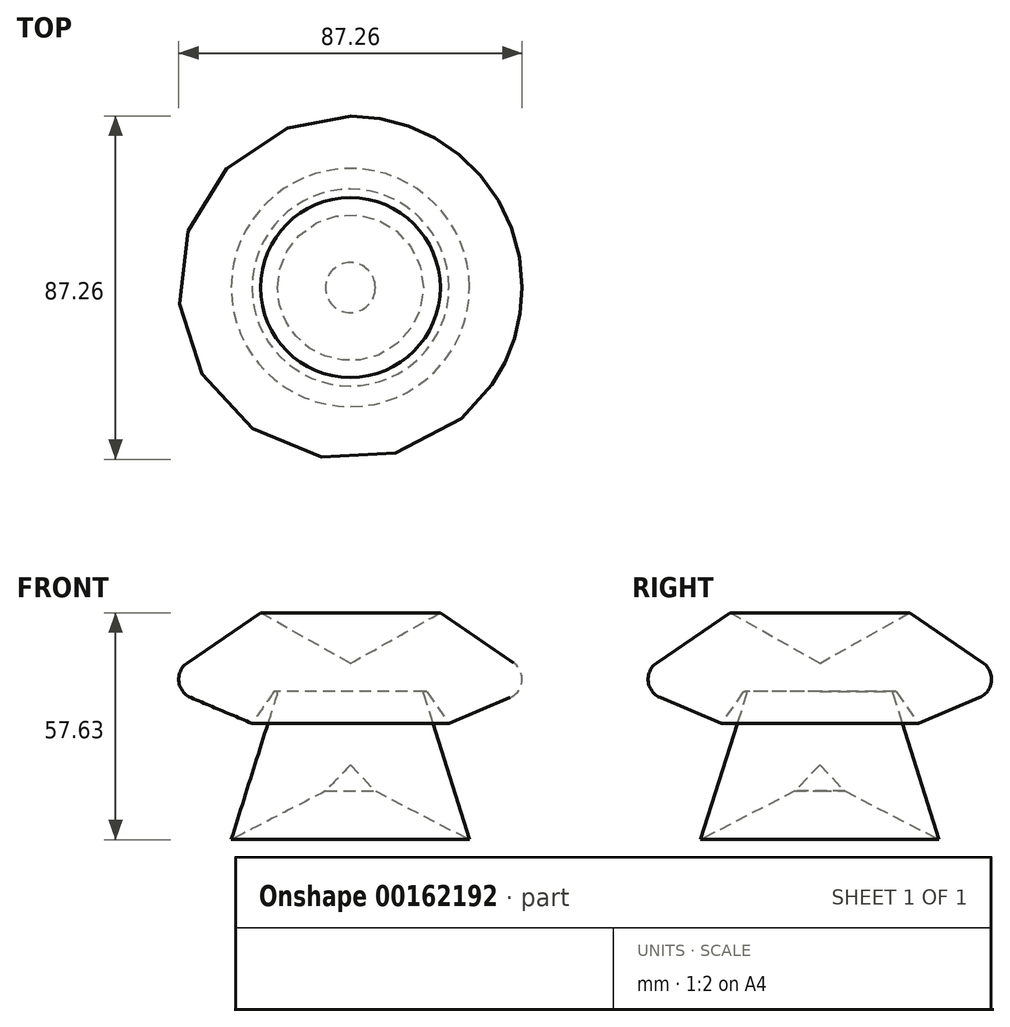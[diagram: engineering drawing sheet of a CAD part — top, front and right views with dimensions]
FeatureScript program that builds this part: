
annotation { "Feature Type Name" : "Feature", "Feature Type Description" : "" }
export const myFeature = defineFeature(function(context is Context, id is Id, definition is map)
    precondition{}
    {
        {
            var Q0;
            Q0=qCreatedBy(makeId("Front.planeOp"),FACE);
            var sketch = newSketch(context, id + "F0", { "sketchPlane" : qUnion([Q0])});
            skLineSegment(sketch, "E0", {"start": v(0, 0) * mm, "end": v(0, 25.82) * mm});
            skLineSegment(sketch, "E1", {"start": v(0, 25.82) * mm, "end": v(-22.83, 38.7) * mm});
            skLineSegment(sketch, "E2", {"start": v(-22.83, 38.7) * mm, "end": v(-49.11, 20.75) * mm});
            skLineSegment(sketch, "E3", {"start": v(-49.11, 20.75) * mm, "end": v(-25, 10.6) * mm});
            skLineSegment(sketch, "E4", {"start": v(-25, 10.6) * mm, "end": v(-17.58, 21.3) * mm});
            skLineSegment(sketch, "E5", {"start": v(-17.58, 21.3) * mm, "end": v(-30.26, -18.94) * mm});
            skLineSegment(sketch, "E6", {"start": v(-30.26, -18.94) * mm, "end": v(-6.34, -6.61) * mm});
            skLineSegment(sketch, "E7", {"start": v(-6.34, -6.61) * mm, "end": v(0, 0) * mm});
            skLineSegment(sketch, "E8", {"start": v(0, 36.15) * mm, "end": v(0, 66.06) * mm, "construction": true});
            skSolve(sketch);
        }
        {
            var Q0;
            Q0=makeQuery(id+"F0.imprint","IMPRINT",FACE,{"disambiguationData":[TD([[makeQuery(id+"F0.imprint","IMPRINT",EDGE,{"derivedFrom":sQuery(id+"F0.wireOp",EDGE,"E0")}),1.0]])]});
            var Q1;
            Q1=sQuery(id+"F0.wireOp",EDGE,"E8");
            revolve(context, id + "F1", {"entities" : qUnion([Q0]), "axis" : qUnion([Q1]), "revolveType" : RevolveType.FULL});
        }
        {
            var Q0;
            Q0=makeQuery(id+"F1.opRevolve","SWEPT_EDGE",EDGE,{"disambiguationData":[OSD([sQuery(id+"F0.wireOp",EDGE,"E2"),sQuery(id+"F0.wireOp",EDGE,"E3")])]});
            fillet(context, id + "F2", {"entities" : qUnion([Q0]), "radius" : 5.08 * mm, "tangentPropagation" : true, "allowEdgeOverflow" : false});
        }
        {
            var Q0;
            Q0=makeQuery(id+"F1.opRevolve","SWEPT_EDGE",EDGE,{"disambiguationData":[OSD([sQuery(id+"F0.wireOp",EDGE,"E4"),sQuery(id+"F0.wireOp",EDGE,"E5")])]});
            fillet(context, id + "F3", {"entities" : qUnion([Q0]), "radius" : 0.5 * mm, "tangentPropagation" : true, "allowEdgeOverflow" : false});
        }
    });
